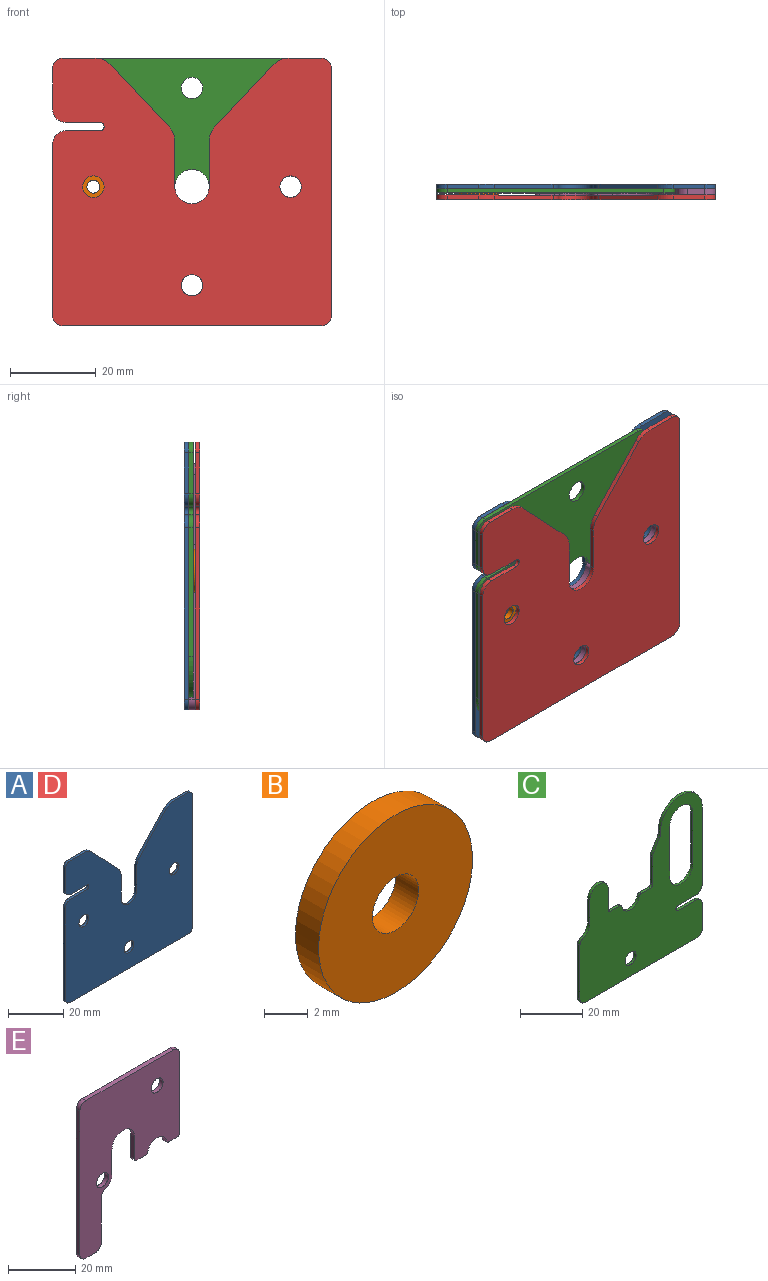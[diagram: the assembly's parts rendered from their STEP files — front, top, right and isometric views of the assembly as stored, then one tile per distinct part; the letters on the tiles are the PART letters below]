
ASSEMBLY  parts=5 mates=4
PART A: 29 faces, bbox 65x1x62.5 mm
  f0: plane 40x1mm, normal (-1,0,0), area 40mm2, adj f1,f2,f16,f27
  f1: plane 65x62.5mm, normal (0,-1,0), area 3414.8mm2, adj f0,f3,f4,f5,f6,f7,f8,f9
  f2: plane 65x62.5mm, normal (0,1,0), area 3414.8mm2, adj f0,f3,f4,f5,f6,f7,f8,f9
  f3: plane 9.5x1mm, normal (-1,0,0), area 9.5mm2, adj f1,f2,f15,f26
  f4: plane 60x1mm, normal (0,0,-1), area 60mm2, adj f1,f2,f16,f17
  f5: plane 57.5x1mm, normal (1,0,0), area 57.5mm2, adj f1,f2,f17,f18
  f6: plane 7.34x1mm, normal (0,0,1), area 7.3mm2, adj f1,f2,f18,f23
  f7: plane 10.51x1mm, normal (-1,0,0), area 10.5mm2, adj f1,f2,f8,f20
  f8: cylinder r=4mm len=8mm, axis (0,1,0), area 12.6mm2, adj f1,f2,f7,f9
  f9: plane 10.51x1mm, normal (1,0,0), area 10.5mm2, adj f1,f2,f8,f21
  f10: plane 14.49x13.66mm, normal (0.73,0,0.69), area 19.9mm2, adj f1,f2,f21,f22
  f11: plane 7.34x1mm, normal (0,0,1), area 7.3mm2, adj f1,f2,f15,f22
  f12: cylinder r=2.5mm len=5mm, axis (0,-1,0), area 15.7mm2, adj f1,f2
  f13: cylinder r=2.5mm len=5mm, axis (0,-1,0), area 15.7mm2, adj f1,f2
  f14: cylinder r=2.5mm len=5mm, axis (0,-1,0), area 15.7mm2, adj f1,f2
  f15: cylinder r=2.5mm len=2.5mm, axis (0,1,0), area 3.9mm2, adj f1,f2,f3,f11
  f16: cylinder r=2.5mm len=2.5mm, axis (0,1,0), area 3.9mm2, adj f0,f1,f2,f4
  f17: cylinder r=2.5mm len=2.5mm, axis (0,-1,0), area 3.9mm2, adj f1,f2,f4,f5
  f18: cylinder r=2.5mm len=2.5mm, axis (0,1,0), area 3.9mm2, adj f1,f2,f5,f6
  f19: plane 14.49x13.66mm, normal (-0.73,0,0.69), area 19.9mm2, adj f1,f2,f20,f23
  f20: cylinder r=5mm len=3.43mm, axis (0,1,0), area 3.8mm2, adj f1,f2,f7,f19
  f21: cylinder r=5mm len=3.43mm, axis (0,-1,0), area 3.8mm2, adj f1,f2,f9,f10
  f22: cylinder r=5mm len=3.64mm, axis (0,-1,0), area 4.1mm2, adj f1,f2,f10,f11
  f23: cylinder r=5mm len=3.64mm, axis (0,1,0), area 4.1mm2, adj f1,f2,f6,f19
  f24: plane 8x1mm, normal (0,0,-1), area 8mm2, adj f1,f2,f26,f28
  f25: plane 8x1mm, normal (0,0,1), area 8mm2, adj f1,f2,f27,f28
  f26: cylinder r=3mm len=3mm, axis (0,1,0), area 4.7mm2, adj f1,f2,f3,f24
  f27: cylinder r=3mm len=3mm, axis (0,1,0), area 4.7mm2, adj f0,f1,f2,f25
  f28: cylinder r=1mm len=2mm, axis (0,1,0), area 3.1mm2, adj f1,f2,f24,f25
PART B: 4 faces, bbox 10x1.5x10 mm
  f0: cylinder r=1.5mm len=3mm, axis (0,1,0), area 14.1mm2, adj f2,f3
  f1: cylinder r=5mm len=10mm, axis (0,1,0), area 47.1mm2, adj f2,f3
  f2: plane 10x10mm, normal (0,-1,0), area 71.5mm2, adj f0,f1
  f3: plane 10x10mm, normal (0,1,0), area 71.5mm2, adj f0,f1
PART C: 36 faces, bbox 55.5x1x59.5 mm
  f0: plane 9.5x1mm, normal (1,0,0), area 9.5mm2, adj f1,f2,f26,f33
  f1: plane 59.5x55.5mm, normal (0,-1,0), area 1957.6mm2, adj f0,f3,f4,f5,f6,f7,f8,f9
  f2: plane 59.5x55.5mm, normal (0,1,0), area 1957.6mm2, adj f0,f3,f4,f5,f6,f7,f8,f9
  f3: plane 20x1mm, normal (1,0,0), area 20mm2, adj f1,f2,f4,f19
  f4: cylinder r=5.25mm len=10.5mm, axis (0,1,0), area 16.5mm2, adj f1,f2,f3,f5
  f5: plane 20x1mm, normal (-1,0,0), area 20mm2, adj f1,f2,f4,f19
  f6: plane 4.1x1mm, normal (0,0,1), area 4.1mm2, adj f1,f2,f27,f30
  f7: plane 8x1mm, normal (1,0,0), area 8mm2, adj f1,f2,f8,f27
  f8: cylinder r=4.25mm len=8.5mm, axis (0,1,0), area 13.4mm2, adj f1,f2,f7,f9
  f9: plane 9x1mm, normal (-1,0,0), area 9mm2, adj f1,f2,f8,f10
  f10: cylinder r=4.5mm len=4.2mm, axis (0,1,0), area 5.4mm2, adj f1,f2,f9,f24
  f11: plane 20.96x1mm, normal (-1,0,0), area 21mm2, adj f1,f2,f24,f25
  f12: plane 50.5x1mm, normal (0,0,-1), area 50.5mm2, adj f1,f2,f25,f26
  f13: plane 30x1mm, normal (1,0,0), area 30mm2, adj f1,f2,f14,f34
  f14: cylinder r=9.5mm len=19mm, axis (0,1,0), area 29.8mm2, adj f1,f2,f13,f15
  f15: plane 1x0.97mm, normal (-1,0,0), area 1mm2, adj f1,f2,f14,f22
  f16: plane 4.65x2.79mm, normal (-0.86,0,0.51), area 5.4mm2, adj f1,f2,f22,f23
  f17: plane 10.81x1mm, normal (-1,0,0), area 10.8mm2, adj f1,f2,f23,f28
  f18: plane 4.1x1mm, normal (0,0,1), area 4.1mm2, adj f1,f2,f28,f29
  f19: cylinder r=5.25mm len=10.5mm, axis (0,1,0), area 16.5mm2, adj f1,f2,f3,f5
  f20: cylinder r=4mm len=7.84mm, axis (0,1,0), area 11mm2, adj f1,f2,f29,f30
  f21: cylinder r=2.5mm len=5mm, axis (0,1,0), area 15.7mm2, adj f1,f2
  f22: cylinder r=2.5mm len=1.29mm, axis (0,-1,0), area 1.4mm2, adj f1,f2,f15,f16
  f23: cylinder r=2.5mm len=1.29mm, axis (0,-1,0), area 1.4mm2, adj f1,f2,f16,f17
  f24: cylinder r=2.5mm len=2.34mm, axis (0,1,0), area 3mm2, adj f1,f2,f10,f11
  f25: cylinder r=2.5mm len=2.5mm, axis (0,1,0), area 3.9mm2, adj f1,f2,f11,f12
  f26: cylinder r=2.5mm len=2.5mm, axis (0,-1,0), area 3.9mm2, adj f0,f1,f2,f12
  f27: cylinder r=1mm len=1mm, axis (0,-1,0), area 1.6mm2, adj f1,f2,f6,f7
  f28: cylinder r=1mm len=1mm, axis (0,-1,0), area 1.6mm2, adj f1,f2,f17,f18
  f29: cylinder r=1mm len=1mm, axis (0,1,0), area 1.4mm2, adj f1,f2,f18,f20
  f30: cylinder r=1mm len=1mm, axis (0,1,0), area 1.4mm2, adj f1,f2,f6,f20
  f31: plane 8x1mm, normal (0,0,1), area 8mm2, adj f1,f2,f33,f35
  f32: plane 8x1mm, normal (0,0,-1), area 8mm2, adj f1,f2,f34,f35
  f33: cylinder r=3mm len=3mm, axis (0,-1,0), area 4.7mm2, adj f0,f1,f2,f31
  f34: cylinder r=3mm len=3mm, axis (0,-1,0), area 4.7mm2, adj f1,f2,f13,f32
  f35: cylinder r=1mm len=2mm, axis (0,-1,0), area 3.1mm2, adj f1,f2,f31,f32
PART D: same geometry as A
PART E: 25 faces, bbox 42x1.5x57.5 mm
  f0: plane 37x1.5mm, normal (0,0,1), area 55.5mm2, adj f14,f15,f16,f17
  f1: plane 52.48x1.5mm, normal (-1,0,0), area 78.7mm2, adj f14,f15,f17,f18
  f2: plane 3.98x1.5mm, normal (0.01,0,-1), area 6mm2, adj f14,f15,f18,f19
  f3: plane 16.35x1.5mm, normal (1,0,0), area 24.5mm2, adj f14,f15,f19,f20
  f4: cylinder r=4mm len=3.81mm, axis (0,1,0), area 7.6mm2, adj f5,f14,f15,f20
  f5: plane 8.88x1.5mm, normal (1,0,0), area 13.3mm2, adj f4,f6,f14,f15
  f6: cylinder r=4.75mm len=9.5mm, axis (0,1,0), area 22.6mm2, adj f5,f7,f14,f15
  f7: plane 8.1x1.5mm, normal (-1,0,0), area 12.1mm2, adj f6,f14,f15,f23
  f8: plane 3.6x1.5mm, normal (0,0,-1), area 5.4mm2, adj f14,f15,f23,f24
  f9: cylinder r=4mm len=7.84mm, axis (0,1,0), area 16.4mm2, adj f14,f15,f21,f24
  f10: plane 3.6x1.5mm, normal (0,0,-1), area 5.4mm2, adj f14,f15,f21,f22
  f11: cylinder r=2.5mm len=5mm, axis (0,1,0), area 23.6mm2, adj f14,f15
  f12: plane 29x1.5mm, normal (1,0,0), area 43.5mm2, adj f14,f15,f16,f22
  f13: cylinder r=2.5mm len=5mm, axis (0,1,0), area 23.6mm2, adj f14,f15
  f14: plane 57.48x42mm, normal (0,-1,0), area 1411.8mm2, adj f0,f1,f2,f3,f4,f5,f6,f7
  f15: plane 57.48x42mm, normal (0,1,0), area 1411.8mm2, adj f0,f1,f2,f3,f4,f5,f6,f7
  f16: cylinder r=2.5mm len=2.5mm, axis (0,1,0), area 5.9mm2, adj f0,f12,f14,f15
  f17: cylinder r=2.5mm len=2.5mm, axis (0,1,0), area 5.9mm2, adj f0,f1,f14,f15
  f18: cylinder r=2.5mm len=2.52mm, axis (0,-1,0), area 5.9mm2, adj f1,f2,f14,f15
  f19: cylinder r=2.5mm len=2.5mm, axis (0,-1,0), area 5.9mm2, adj f2,f3,f14,f15
  f20: cylinder r=2.5mm len=2.38mm, axis (0,1,0), area 4.7mm2, adj f3,f4,f14,f15
  f21: cylinder r=1mm len=1.5mm, axis (0,1,0), area 2.1mm2, adj f9,f10,f14,f15
  f22: cylinder r=1mm len=1.5mm, axis (0,-1,0), area 2.4mm2, adj f10,f12,f14,f15
  f23: cylinder r=1mm len=1.5mm, axis (0,-1,0), area 2.4mm2, adj f7,f8,f14,f15
  f24: cylinder r=1mm len=1.5mm, axis (0,1,0), area 2.1mm2, adj f8,f9,f14,f15
PLACE A t=(38.25,30.29,12.82)mm fixed
PLACE B t=(15.25,29.29,12.82)mm
PLACE C rot(axis=(0,1,0),180deg) t=(38.25,29.29,12.82)mm
PLACE D t=(38.25,27.79,12.82)mm
PLACE E rot(axis=(0,1,0),180deg) t=(38.25,29.29,12.82)mm
MATE fastened B.f0 <-> A.f13  axis (0,1,0) through (15.25,29.29,12.82)mm
MATE fastened E.f13 <-> A.f14  axis (0,1,0) through (61.25,29.29,12.82)mm
MATE fastened D.f14 <-> E.f13  axis (0,1,0) through (61.25,27.79,12.82)mm
MATE cylindrical C.f19 <-> B.f1  axis (0,1,0) through (15.25,29.29,12.82)mm
